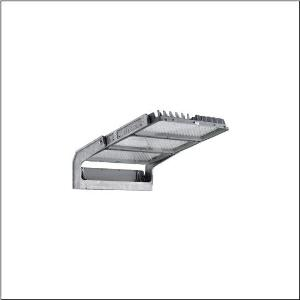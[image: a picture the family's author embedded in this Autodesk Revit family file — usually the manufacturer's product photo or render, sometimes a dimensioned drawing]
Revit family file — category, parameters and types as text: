
# Revit family: floodlight_fl_11_maxi_pro___rs07_5xa779228k01gb_83e5
name_source: partatom
category: Lighting Fixtures
units: mm (PartAtom-declared; Revit-internal decimal feet)

## family parameters
Cut with Voids When Loaded = No
Host = Face
Light Source = No
Part Type = Normal
Room Calculation Point = No
Round Connector Dimension = Use Diameter
Shared = No

## types (1)
- --- (1 x LED, 149760 lm, 1285.1 W, 5700K)
    Apparent Load = 1285 VA
    CIE Flux Codes = 80 93 99 100 99
    Color Rendering = 80
    Color Temperature = 5700K
    Default Elevation = 1800 mm
    Description = Floodlight FL 11  maxi  pro floodlight; light control with lens of PMMA; cover panel of toughened safety glass, transparent; light distribution: RS07, rotationally symmetric direct distribution, LED; colour temperature: 5700K, rated luminous flux: 149.760lm, colour rendering: CRI > 80, light colour: 857; luminous efficacy: 117lm/W; brightness control: DMX+RDM; with terminal, 5-pole, max. 2.5mm², mains connection: 220..240V/380..400V AC, 50/60Hz, surge voltage resistance: line to ground: 10kV, LED service life up to 100,000h L90. Typical operating time: 1000h per year., ECG replaceable separately, LED unit replaceable without ESD environment, dustproof LED module, dimming range 10..100%; 1285W floodlight with 3x LED unit of diecast aluminium, coated grey; length: 1.003mm / width: 651mm / height: 338mm; mounting bracket, of diecast aluminium, uncoated, natural, equipment: Power, protection rating (complete): IP66; insulation class (complete): insulation class I (protective earthing); certification: CE, ENEC, VDE; ball protection: ball impact resistant, only for outdoor installations in the designated locations, permissible operating ambient temperature: -45..+55°C, permissible storage temperature: -40..+85°Cpackaging unit: 1 piece

Light Distribution: RS07
    Height = 320 mm
    Lamp = 1 x LED
    Lamp Light Flux = 149760 lm
    Lamp Power = 1285.1 W
    Lamp count = 1
    Length = 1002 mm
    Luminous efficacy = 117 lm/W
    Manufacturer = Siteco
    ModVariant = No
    Model = 5XA779228K01GB
    Mounting Place = Ceiling
    Mounting Type = Surface mounted
    Number of Poles = 1
    OnlyDefault = Yes
    Power Factor = 1
    Product Name = Floodlight FL 11 maxi pro | RS07
    Product group = floodlight | ceiling mounted
    ProductGroupID = 303
    Protection Class = Protection class I
    Protection Degree = IP 66
    RLX_Detail_Level = 1
    RLX_Emergency_Light_Flux = 0 lm
    RLX_Emergency_Type = 0
    RLX_Emergency_Type_DB = No
    RlxData = <blob elided: 40237 chars, md5=bf4d3aee>
    Socket = socket
    Standby Power = 0 W
    System Light Flux = 149760 lm
    System Power = 1285 W
    Type Comments = factory setting: luminous flux: 100 % | dim-lin: 255 | 875 mA
    Type Image = l_1356210.jpg
    URL = http://relux.com
    VarID = @adj_033383
    Voltage = 0 V
    Weight = 0.00 kg
    Width = 655 mm

## geometry (parser evidence)
native form markers: Blend x4, Sweep x13
no freeform markers — native parametric forms only
